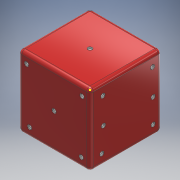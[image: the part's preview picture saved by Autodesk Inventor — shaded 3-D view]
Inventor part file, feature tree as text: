
AUTODESK INVENTOR PART (.ipt)
format: ipt  version: 2018 (Build 220112000, 112)  size: 340,480 bytes
history: native  units: mm
features: fillet x26, sketch x23, hole x21, extrude x1
ambient origin geometry x8: Origin, YZ Plane, XZ Plane, XY Plane, X Axis, Y Axis, Z Axis, Center Point
bodies: Solid1 (feature_tree)
feature tree (71):
  extrude  "Extrusion1"  Depth=10.0mm
  fillet  "Fillet1"  Radius=10.0mm
  fillet  "Fillet2"  Radius=0.5mm
  fillet  "Fillet3"  Radius=0.5mm
  fillet  "Fillet4"  Radius=0.5mm
  fillet  "Fillet5"  Radius=0.5mm
  hole  "Hole1"  [1 undecoded]
  sketch  "Sketch3"  dims[d9=0.5mm d10=6.0mm d11=3.023mm d12=2.0mm d13=14.3117mm d14=0.2mm d15=20.594885mm d16=0.5mm]
  hole  "Hole2"  [1 undecoded]
  hole  "Hole3"  [1 undecoded]
  hole  "Hole4"  [1 undecoded]
  hole  "Hole5"  [1 undecoded]
  hole  "Hole6"  [1 undecoded]
  hole  "Hole7"  [1 undecoded]
  hole  "Hole8"  [1 undecoded]
  hole  "Hole9"  [1 undecoded]
  hole  "Hole10"  [1 undecoded]
  hole  "Hole11"  [1 undecoded]
  hole  "Hole12"  [1 undecoded]
  hole  "Hole13"  [1 undecoded]
  hole  "Hole14"  [1 undecoded]
  hole  "Hole15"  [1 undecoded]
  hole  "Hole16"  [1 undecoded]
  hole  "Hole17"  [1 undecoded]
  hole  "Hole18"  [1 undecoded]
  hole  "Hole19"  [1 undecoded]
  hole  "Hole20"  [1 undecoded]
  hole  "Hole21"  [1 undecoded]
  fillet  "Fillet6"  Radius=0.05mm
  fillet  "Fillet7"  Radius=0.05mm
  fillet  "Fillet8"  Radius=0.05mm
  fillet  "Fillet9"  Radius=0.05mm
  fillet  "Fillet10"  Radius=0.05mm
  fillet  "Fillet11"  Radius=0.05mm
  fillet  "Fillet12"  Radius=0.05mm
  fillet  "Fillet13"  Radius=0.05mm
  fillet  "Fillet14"  Radius=0.05mm
  fillet  "Fillet15"  Radius=0.05mm
  fillet  "Fillet16"  Radius=0.05mm
  fillet  "Fillet17"  Radius=0.05mm
  fillet  "Fillet18"  Radius=0.05mm
  fillet  "Fillet19"  Radius=0.05mm
  fillet  "Fillet20"  Radius=0.05mm
  fillet  "Fillet21"  Radius=0.05mm
  fillet  "Fillet22"  Radius=0.05mm
  fillet  "Fillet23"  Radius=0.05mm
  fillet  "Fillet24"  Radius=0.05mm
  fillet  "Fillet25"  Radius=0.05mm
  fillet  "Fillet26"  [1 undecoded]
  sketch  "Sketch1"  dims[d0=10.0mm d1=10.0mm d2=10.0mm d3=0.0mm d4=0.5mm d5=0.5mm d6=0.5mm d7=0.5mm]
  sketch  "Sketch2"  dims[d8=0.5mm]
  sketch  "Sketch4"  dims[d17=0.5mm]
  sketch  "Sketch5"  dims[d18=0.5mm d19=6.0mm d20=3.023mm d21=2.0mm d22=14.3117mm d23=0.2mm d24=20.594885mm d25=0.5mm]
  sketch  "Sketch6"  dims[d26=0.5mm d27=6.0mm d28=3.023mm d29=2.0mm d30=14.3117mm d31=0.2mm d32=20.594885mm d33=0.5mm]
  sketch  "Sketch7"  dims[d34=0.5mm]
  sketch  "Sketch8"  dims[d35=0.5mm d36=6.0mm d37=3.023mm d38=2.0mm d39=14.3117mm d40=0.2mm d41=20.594885mm d42=0.5mm]
  sketch  "Sketch9"  dims[d43=0.5mm d44=6.0mm d45=3.023mm d46=2.0mm d47=14.3117mm d48=0.2mm d49=20.594885mm d50=0.5mm]
  sketch  "Sketch10"  dims[d51=0.5mm d52=6.0mm d53=3.023mm d54=2.0mm d55=14.3117mm d56=0.2mm d57=20.594885mm d58=0.5mm]
  sketch  "Sketch11"  dims[d59=0.5mm d60=6.0mm d61=3.023mm d62=2.0mm d63=14.3117mm d64=0.2mm d65=20.594885mm d66=0.5mm]
  sketch  "Sketch12"  dims[d67=0.5mm d68=6.0mm d69=3.023mm d70=2.0mm d71=14.3117mm d72=0.2mm d73=20.594885mm d74=0.5mm]
  sketch  "Sketch13"  dims[d75=0.5mm d76=6.0mm d77=3.023mm d78=2.0mm d79=14.3117mm d80=0.2mm d81=20.594885mm d82=0.5mm]
  sketch  "Sketch14"  dims[d83=0.5mm d84=6.0mm d85=3.023mm d86=2.0mm d87=14.3117mm d88=0.2mm d89=20.594885mm d90=0.5mm]
  sketch  "Sketch15"  dims[d91=0.5mm d92=6.0mm d93=3.023mm d94=2.0mm d95=14.3117mm d96=0.2mm d97=20.594885mm d98=0.5mm]
  sketch  "Sketch16"  dims[d99=0.5mm d100=6.0mm d101=3.023mm d102=2.0mm d103=14.3117mm d104=0.2mm d105=20.594885mm d106=0.5mm]
  sketch  "Sketch17"  dims[d107=0.5mm d108=6.0mm d109=3.023mm d110=2.0mm d111=14.3117mm d112=0.2mm d113=20.594885mm d114=0.5mm]
  sketch  "Sketch18"  dims[d115=0.5mm d116=6.0mm d117=3.023mm d118=2.0mm d119=14.3117mm d120=0.2mm d121=20.594885mm d122=0.5mm]
  sketch  "Sketch19"  dims[d123=0.5mm d124=6.0mm d125=3.023mm d126=2.0mm d127=14.3117mm d128=0.2mm d129=20.594885mm d130=0.5mm]
  sketch  "Sketch20"  dims[d131=0.5mm d132=6.0mm d133=3.023mm d134=2.0mm d135=14.3117mm d136=0.2mm d137=20.594885mm d138=0.5mm]
  sketch  "Sketch21"  dims[d139=0.5mm d140=6.0mm d141=3.023mm d142=2.0mm d143=14.3117mm d144=0.2mm d145=20.594885mm d146=0.5mm]
  sketch  "Sketch22"  dims[d147=0.5mm d148=6.0mm d149=3.023mm d150=2.0mm d151=14.3117mm d152=0.2mm d153=20.594885mm d154=0.5mm]
  sketch  "Sketch23"  dims[d155=0.5mm d156=6.0mm d157=3.023mm d158=2.0mm d159=14.3117mm d160=0.2mm d161=20.594885mm d162=0.5mm d163=0.5mm d164=6.0mm d165=3.023mm d166=2.0mm d167=14.3117mm d168=0.2mm d169=20.594885mm d170=0.5mm d171=0.5mm d172=6.0mm d173=3.023mm d174=2.0mm d175=14.3117mm d176=0.2mm d177=20.594885mm d178=0.05mm d179=0.05mm d180=0.05mm d181=0.05mm d182=0.05mm d183=0.05mm d184=0.05mm d185=0.05mm d186=0.05mm d187=0.05mm d188=0.05mm d189=0.05mm d190=0.05mm d191=0.05mm d192=0.05mm d193=0.05mm d194=0.05mm d195=0.05mm d196=0.05mm d197=0.05mm d198=0.05mm]
note: 22 required parameter values undecoded (feature->parameter linkage not recoverable at this tier; creation-order binding heuristic only, values carry confidence <= 0.55)
